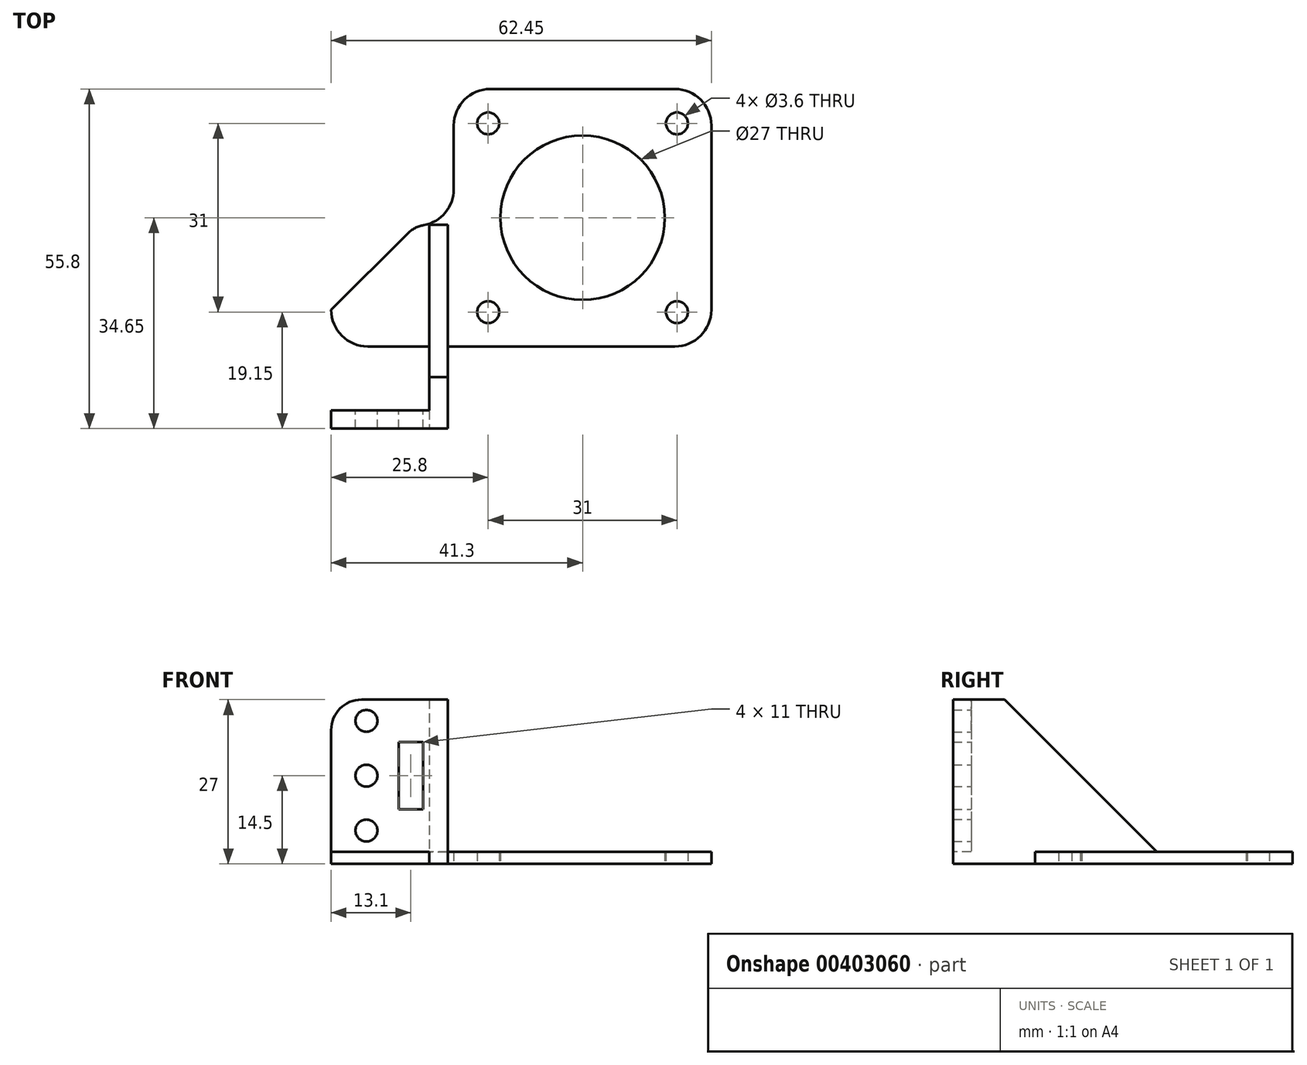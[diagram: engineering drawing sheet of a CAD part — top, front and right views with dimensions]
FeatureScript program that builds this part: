
annotation { "Feature Type Name" : "Feature", "Feature Type Description" : "" }
export const myFeature = defineFeature(function(context is Context, id is Id, definition is map)
    precondition{}
    {
        {
            var Q0;
            Q0=qCreatedBy(makeId("Top.planeOp"),FACE);
            var sketch = newSketch(context, id + "F0", { "sketchPlane" : qUnion([Q0])});
            skLineSegment(sketch, "E0.bottom", {"start": v(21.15, 21.15) * mm, "end": v(-21.15, 21.15) * mm});
            skLineSegment(sketch, "E0.top", {"start": v(21.15, -21.15) * mm, "end": v(-21.15, -21.15) * mm});
            skLineSegment(sketch, "E0.left", {"start": v(21.15, 21.15) * mm, "end": v(21.15, -21.15) * mm});
            skLineSegment(sketch, "E0.right", {"start": v(-21.15, 21.15) * mm, "end": v(-21.15, -21.15) * mm});
            skPoint(sketch, "E0.middle", {"position": v(0, 0) * mm});
            skLineSegment(sketch, "E1.bottom", {"start": v(15.5, 15.5) * mm, "end": v(-15.5, 15.5) * mm, "construction": true});
            skLineSegment(sketch, "E1.top", {"start": v(15.5, -15.5) * mm, "end": v(-15.5, -15.5) * mm, "construction": true});
            skLineSegment(sketch, "E1.left", {"start": v(15.5, 15.5) * mm, "end": v(15.5, -15.5) * mm, "construction": true});
            skLineSegment(sketch, "E1.right", {"start": v(-15.5, 15.5) * mm, "end": v(-15.5, -15.5) * mm, "construction": true});
            skCircle(sketch, "E2", {"center": v(-15.5, 15.5) * mm, "radius": 1.8 * mm});
            skCircle(sketch, "E3", {"center": v(15.5, 15.5) * mm, "radius": 1.8 * mm});
            skCircle(sketch, "E4", {"center": v(15.5, -15.5) * mm, "radius": 1.8 * mm});
            skCircle(sketch, "E5", {"center": v(-15.5, -15.5) * mm, "radius": 1.8 * mm});
            skCircle(sketch, "E6", {"center": v(0, 0) * mm, "radius": 13.5 * mm});
            skLineSegment(sketch, "E7.bottom", {"start": v(-21.15, -21.15) * mm, "end": v(-41.3, -21.15) * mm});
            skLineSegment(sketch, "E7.top", {"start": v(-21.15, -1.15) * mm, "end": v(-41.3, -1.15) * mm});
            skLineSegment(sketch, "E7.left", {"start": v(-21.15, -21.15) * mm, "end": v(-21.15, -1.15) * mm});
            skLineSegment(sketch, "E7.right", {"start": v(-41.3, -21.15) * mm, "end": v(-41.3, -1.15) * mm});
            skLineSegment(sketch, "E8.bottom", {"start": v(-41.3, -21.15) * mm, "end": v(-21.16, -21.15) * mm});
            skLineSegment(sketch, "E8.top", {"start": v(-41.3, -34.65) * mm, "end": v(-21.16, -34.65) * mm});
            skLineSegment(sketch, "E8.left", {"start": v(-41.3, -21.15) * mm, "end": v(-41.3, -34.65) * mm});
            skLineSegment(sketch, "E8.right", {"start": v(-21.16, -21.15) * mm, "end": v(-21.16, -34.65) * mm});
            skSolve(sketch);
        }
        {
            var Q0;
            Q0=makeQuery(id+"F0.imprint","IMPRINT",FACE,{"disambiguationData":[TD([[makeQuery(id+"F0.imprint","IMPRINT",EDGE,{"derivedFrom":sQuery(id+"F0.wireOp",EDGE,"E0.bottom")}),1.0]])]});
            var Q1;
            Q1=makeQuery(id+"F0.imprint","IMPRINT",FACE,{"disambiguationData":[TD([[makeQuery(id+"F0.imprint","IMPRINT",EDGE,{"derivedFrom":sQuery(id+"F0.wireOp",EDGE,"E7.bottom")}),-1.0]])]});
            var Q2;
            Q2=makeQuery(id+"F0.imprint","IMPRINT",FACE,{"disambiguationData":[TD([[makeQuery(id+"F0.imprint","IMPRINT",EDGE,{"derivedFrom":sQuery(id+"F0.wireOp",EDGE,"E8.bottom")}),-1.0]])]});
            extrude(context, id + "F1", {"entities" : qUnion([Q0, Q1, Q2]), "depth" : 2 * mm});
        }
        {
            var Q0;
            Q0=qCreatedBy(makeId("Top.planeOp"),FACE);
            var sketch = newSketch(context, id + "F2", { "sketchPlane" : qUnion([Q0])});
            skLineSegment(sketch, "E9.bottom", {"start": v(-22.16, -1.15) * mm, "end": v(-25.16, -1.15) * mm});
            skLineSegment(sketch, "E9.top", {"start": v(-22.16, -34.65) * mm, "end": v(-25.16, -34.65) * mm});
            skLineSegment(sketch, "E9.left", {"start": v(-22.16, -1.15) * mm, "end": v(-22.16, -34.65) * mm});
            skLineSegment(sketch, "E9.right", {"start": v(-25.16, -1.15) * mm, "end": v(-25.16, -34.65) * mm});
            skSolve(sketch);
        }
        {
            var Q0;
            Q0=qSketchRegion(id+"F2",true);
            extrude(context, id + "F3", {"entities" : qUnion([Q0]), "operationType" : NewBodyOperationType.ADD, "depth" : 27 * mm});
        }
        {
            var Q0;
            {var subQ0=sQuery(id+"F0.wireOp",EDGE,"E8.left");var subQ1=sQuery(id+"F0.wireOp",EDGE,"E7.right");var subQ2=sQuery(id+"F0.wireOp",EDGE,"E8.top");var subQ3=sQuery(id+"F0.wireOp",EDGE,"E7.top");Q0=makeQuery(id+"F3.boolean.opBoolean","SPLIT",FACE,{"disambiguationData":[TD([makeQuery(id+"F3.opExtrude","SWEPT_FACE",FACE,{"disambiguationData":[OSD([sQuery(id+"F2.wireOp",EDGE,"E9.right")])]})])],"derivedFrom":makeQuery(id+"F1.opExtrude","CAP_FACE",FACE,{"disambiguationData":[OSD([sQuery(id+"F0.wireOp",EDGE,"E0.bottom"),sQuery(id+"F0.wireOp",EDGE,"E0.top"),sQuery(id+"F0.wireOp",EDGE,"E0.left"),sQuery(id+"F0.wireOp",EDGE,"E0.right"),sQuery(id+"F0.wireOp",EDGE,"E2"),sQuery(id+"F0.wireOp",EDGE,"E3"),sQuery(id+"F0.wireOp",EDGE,"E4"),sQuery(id+"F0.wireOp",EDGE,"E5"),sQuery(id+"F0.wireOp",EDGE,"E6"),sQuery(id+"F0.wireOp",EDGE,"E7.bottom"),subQ3,subQ1,subQ2,subQ0,sQuery(id+"F0.wireOp",EDGE,"E8.right")])],"isStart":false})});}
            var sketch = newSketch(context, id + "F4", { "sketchPlane" : qUnion([Q0])});
            skLineSegment(sketch, "E10.bottom", {"start": v(-41.3, -31.65) * mm, "end": v(-25.16, -31.65) * mm});
            skLineSegment(sketch, "E10.top", {"start": v(-41.3, -34.65) * mm, "end": v(-25.16, -34.65) * mm});
            skLineSegment(sketch, "E10.left", {"start": v(-41.3, -31.65) * mm, "end": v(-41.3, -34.65) * mm});
            skLineSegment(sketch, "E10.right", {"start": v(-25.16, -31.65) * mm, "end": v(-25.16, -34.65) * mm});
            skSolve(sketch);
        }
        {
            var Q0;
            Q0=makeQuery(id+"F4.imprint","IMPRINT",FACE,{"disambiguationData":[TD([[makeQuery(id+"F4.imprint","IMPRINT",EDGE,{"derivedFrom":sQuery(id+"F4.wireOp",EDGE,"E10.bottom")}),-1.0]])]});
            extrude(context, id + "F5", {"entities" : qUnion([Q0]), "operationType" : NewBodyOperationType.ADD, "depth" : 25 * mm});
        }
        {
            var Q0;
            Q0=makeQuery(id+"F5.opExtrude","SWEPT_FACE",FACE,{"disambiguationData":[OSD([sQuery(id+"F4.wireOp",EDGE,"E10.bottom")])]});
            var sketch = newSketch(context, id + "F6", { "sketchPlane" : qUnion([Q0])});
            skCircle(sketch, "E11", {"center": v(35.5, 14.5) * mm, "radius": 1.8 * mm});
            skCircle(sketch, "E12", {"center": v(35.5, 5.5) * mm, "radius": 1.8 * mm});
            skCircle(sketch, "E13", {"center": v(35.5, 23.5) * mm, "radius": 1.8 * mm});
            skLineSegment(sketch, "E14.bottom", {"start": v(30.2, 20) * mm, "end": v(26.2, 20) * mm});
            skLineSegment(sketch, "E14.top", {"start": v(30.2, 9) * mm, "end": v(26.2, 9) * mm});
            skLineSegment(sketch, "E14.left", {"start": v(30.2, 20) * mm, "end": v(30.2, 9) * mm});
            skLineSegment(sketch, "E14.right", {"start": v(26.2, 20) * mm, "end": v(26.2, 9) * mm});
            skSolve(sketch);
        }
        {
            var Q0;
            Q0=makeQuery(id+"F6.imprint","IMPRINT",FACE,{"disambiguationData":[TD([[makeQuery(id+"F6.imprint","IMPRINT",EDGE,{"derivedFrom":sQuery(id+"F6.wireOp",EDGE,"E11")}),1.0]])]});
            var Q1;
            Q1=makeQuery(id+"F6.imprint","IMPRINT",FACE,{"disambiguationData":[TD([[makeQuery(id+"F6.imprint","IMPRINT",EDGE,{"derivedFrom":sQuery(id+"F6.wireOp",EDGE,"E12")}),1.0]])]});
            var Q2;
            Q2=makeQuery(id+"F6.imprint","IMPRINT",FACE,{"disambiguationData":[TD([[makeQuery(id+"F6.imprint","IMPRINT",EDGE,{"derivedFrom":sQuery(id+"F6.wireOp",EDGE,"E13")}),1.0]])]});
            var Q3;
            Q3=makeQuery(id+"F6.imprint","IMPRINT",FACE,{"disambiguationData":[TD([[makeQuery(id+"F6.imprint","IMPRINT",EDGE,{"derivedFrom":sQuery(id+"F6.wireOp",EDGE,"E14.bottom")}),1.0]])]});
            extrude(context, id + "F7", {"entities" : qUnion([Q0, Q1, Q2, Q3]), "operationType" : NewBodyOperationType.REMOVE, "oppositeDirection" : true, "depth" : 25 * mm});
        }
        {
            var Q0;
            Q0=makeQuery(id+"F3.opExtrude","CAP_EDGE",EDGE,{"disambiguationData":[OSD([sQuery(id+"F2.wireOp",EDGE,"E9.bottom")])],"isStart":false});
            chamfer(context, id + "F8", {"entities" : qUnion([Q0]), "width" : 25 * mm, "tangentPropagation" : true});
        }
        {
            var Q0;
            Q0=makeQuery(id+"F1.opExtrude","SWEPT_EDGE",EDGE,{"disambiguationData":[OSD([sQuery(id+"F0.wireOp",EDGE,"E7.top"),sQuery(id+"F0.wireOp",EDGE,"E7.right")])]});
            chamfer(context, id + "F9", {"entities" : qUnion([Q0]), "width" : 14 * mm, "tangentPropagation" : true});
        }
        {
            var Q0;
            {var subQ0=sQuery(id+"F0.wireOp",EDGE,"E7.right");Q0=makeQuery(id+"F9.opChamfer","BLEND_EDGE",EDGE,{"blendedFrom":[makeQuery(id+"F1.opExtrude","SWEPT_EDGE",EDGE,{"disambiguationData":[OSD([sQuery(id+"F0.wireOp",EDGE,"E7.top"),subQ0])]}),makeQuery(id+"F5.boolean.opBoolean","MERGE",FACE,{"derivedFrom":[makeQuery(id+"F1.opExtrude","SWEPT_FACE",FACE,{"disambiguationData":[OSD([subQ0,sQuery(id+"F0.wireOp",EDGE,"E8.left")])]}),makeQuery(id+"F5.opExtrude","SWEPT_FACE",FACE,{"disambiguationData":[OSD([sQuery(id+"F4.wireOp",EDGE,"E10.left")])]})]})],"blendedInto":[makeQuery(id+"F5.boolean.opBoolean","MERGE",FACE,{"derivedFrom":[makeQuery(id+"F1.opExtrude","SWEPT_FACE",FACE,{"disambiguationData":[OSD([subQ0,sQuery(id+"F0.wireOp",EDGE,"E8.left")])]}),makeQuery(id+"F5.opExtrude","SWEPT_FACE",FACE,{"disambiguationData":[OSD([sQuery(id+"F4.wireOp",EDGE,"E10.left")])]})]})]});}
            var Q1;
            {var subQ0=sQuery(id+"F0.wireOp",EDGE,"E7.top");Q1=makeQuery(id+"F9.opChamfer","BLEND_EDGE",EDGE,{"blendedFrom":[makeQuery(id+"F1.opExtrude","SWEPT_EDGE",EDGE,{"disambiguationData":[OSD([subQ0,sQuery(id+"F0.wireOp",EDGE,"E7.right")])]}),makeQuery(id+"F3.boolean.opBoolean","MERGE",FACE,{"derivedFrom":[makeQuery(id+"F1.opExtrude","SWEPT_FACE",FACE,{"disambiguationData":[OSD([subQ0])]}),makeQuery(id+"F3.opExtrude","SWEPT_FACE",FACE,{"disambiguationData":[OSD([sQuery(id+"F2.wireOp",EDGE,"E9.bottom")])]})]})],"blendedInto":[makeQuery(id+"F3.boolean.opBoolean","MERGE",FACE,{"derivedFrom":[makeQuery(id+"F1.opExtrude","SWEPT_FACE",FACE,{"disambiguationData":[OSD([subQ0])]}),makeQuery(id+"F3.opExtrude","SWEPT_FACE",FACE,{"disambiguationData":[OSD([sQuery(id+"F2.wireOp",EDGE,"E9.bottom")])]})]})]});}
            var Q2;
            Q2=makeQuery(id+"F1.opExtrude","SWEPT_EDGE",EDGE,{"disambiguationData":[OSD([sQuery(id+"F0.wireOp",EDGE,"E8.top"),sQuery(id+"F0.wireOp",EDGE,"E8.right")])]});
            var Q3;
            Q3=makeQuery(id+"F5.opExtrude","CAP_EDGE",EDGE,{"disambiguationData":[OSD([sQuery(id+"F4.wireOp",EDGE,"E10.left")])],"isStart":false});
            fillet(context, id + "F10", {"entities" : qUnion([Q0, Q1, Q2, Q3]), "radius" : 5 * mm, "tangentPropagation" : true, "allowEdgeOverflow" : false});
        }
        {
            var Q0;
            Q0=makeQuery(id+"F1.opExtrude","SWEPT_EDGE",EDGE,{"disambiguationData":[OSD([sQuery(id+"F0.wireOp",EDGE,"E0.top"),sQuery(id+"F0.wireOp",EDGE,"E0.left")])]});
            var Q1;
            Q1=makeQuery(id+"F1.opExtrude","SWEPT_EDGE",EDGE,{"disambiguationData":[OSD([sQuery(id+"F0.wireOp",EDGE,"E0.bottom"),sQuery(id+"F0.wireOp",EDGE,"E0.left")])]});
            var Q2;
            Q2=makeQuery(id+"F1.opExtrude","SWEPT_EDGE",EDGE,{"disambiguationData":[OSD([sQuery(id+"F0.wireOp",EDGE,"E0.bottom"),sQuery(id+"F0.wireOp",EDGE,"E0.right")])]});
            var Q3;
            Q3=makeQuery(id+"F1.opExtrude","SWEPT_EDGE",EDGE,{"disambiguationData":[OSD([sQuery(id+"F0.wireOp",EDGE,"E0.right"),sQuery(id+"F0.wireOp",EDGE,"E7.top"),sQuery(id+"F0.wireOp",EDGE,"E7.left")])]});
            var Q4;
            Q4=makeQuery(id+"F1.opExtrude","SWEPT_EDGE",EDGE,{"disambiguationData":[OSD([sQuery(id+"F0.wireOp",EDGE,"E7.bottom"),sQuery(id+"F0.wireOp",EDGE,"E8.bottom"),sQuery(id+"F0.wireOp",EDGE,"E8.right")])]});
            fillet(context, id + "F11", {"entities" : qUnion([Q0, Q1, Q2, Q3, Q4]), "radius" : 6 * mm, "tangentPropagation" : true, "allowEdgeOverflow" : false});
        }
    });
